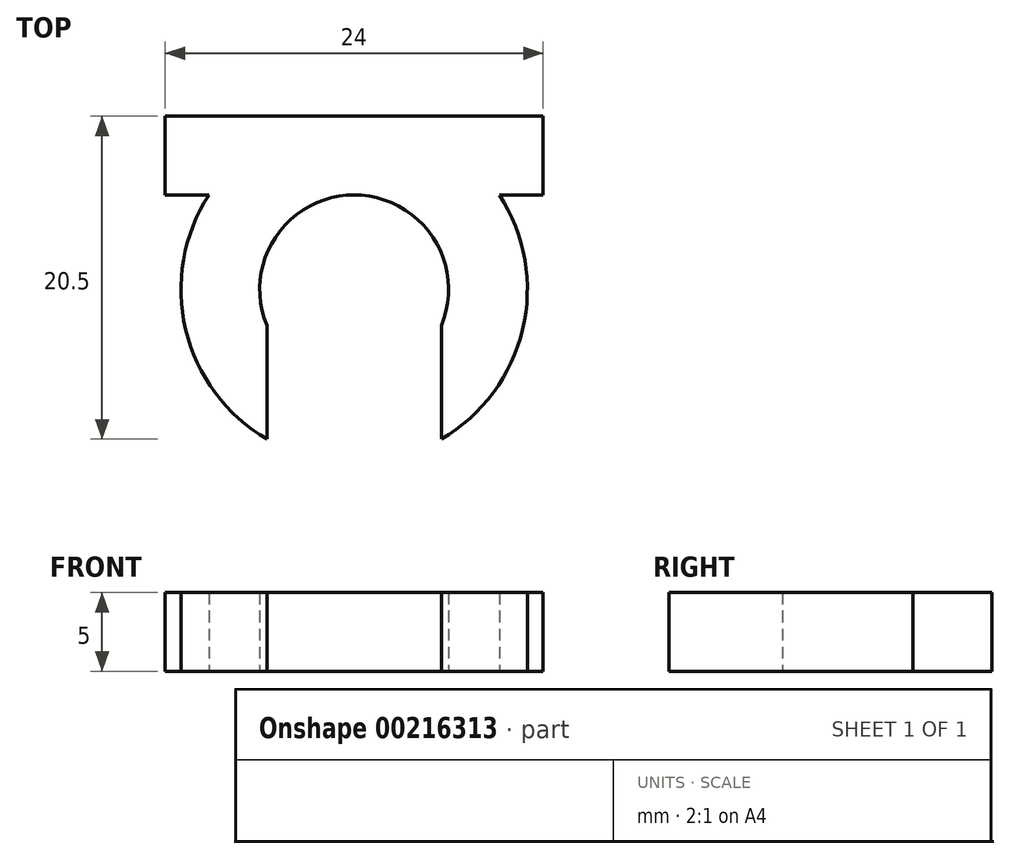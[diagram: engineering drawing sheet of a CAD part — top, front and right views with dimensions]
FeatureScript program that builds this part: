
annotation { "Feature Type Name" : "Feature", "Feature Type Description" : "" }
export const myFeature = defineFeature(function(context is Context, id is Id, definition is map)
    precondition{}
    {
        {
            var Q0;
            Q0=qCreatedBy(makeId("Top.planeOp"),FACE);
            var sketch = newSketch(context, id + "F0", { "sketchPlane" : qUnion([Q0])});
            skLineSegment(sketch, "E0", {"start": v(-5.54, -2.3) * mm, "end": v(0, 0) * mm, "construction": true});
            skLineSegment(sketch, "E1", {"start": v(0, 0) * mm, "end": v(5.54, -2.3) * mm, "construction": true});
            skLineSegment(sketch, "E2", {"start": v(0, 0) * mm, "end": v(0, -7.2) * mm, "construction": true});
            skArc(sketch, "E3", {"start": v(5.54, -2.3) * mm, "mid": v(0, 6) * mm, "end": v(-5.54, -2.3) * mm});
            skArc(sketch, "E4", {"start": v(5.54, -9.5) * mm, "mid": v(0, 11) * mm, "end": v(-5.54, -9.5) * mm});
            skLineSegment(sketch, "E5", {"start": v(5.54, -2.3) * mm, "end": v(5.54, -9.5) * mm});
            skLineSegment(sketch, "E6", {"start": v(-5.54, -2.3) * mm, "end": v(-5.54, -9.5) * mm});
            skPoint(sketch, "E7.firstSnap0", {"position": v(0, 11) * mm});
            skPoint(sketch, "E7.oppositeSnap0", {"position": v(0, 6) * mm});
            skLineSegment(sketch, "E7.bottom", {"start": v(-12, 11) * mm, "end": v(12, 11) * mm});
            skLineSegment(sketch, "E7.top", {"start": v(-12, 6) * mm, "end": v(12, 6) * mm});
            skLineSegment(sketch, "E7.left", {"start": v(-12, 11) * mm, "end": v(-12, 6) * mm});
            skLineSegment(sketch, "E7.right", {"start": v(12, 11) * mm, "end": v(12, 6) * mm});
            skSolve(sketch);
        }
        {
            var Q0;
            Q0 = qSketchRegion(id + "F0", true);
            extrude(context, id + "F1", {"entities" : qUnion([Q0]), "depth" : 5 * mm});
        }
    });
